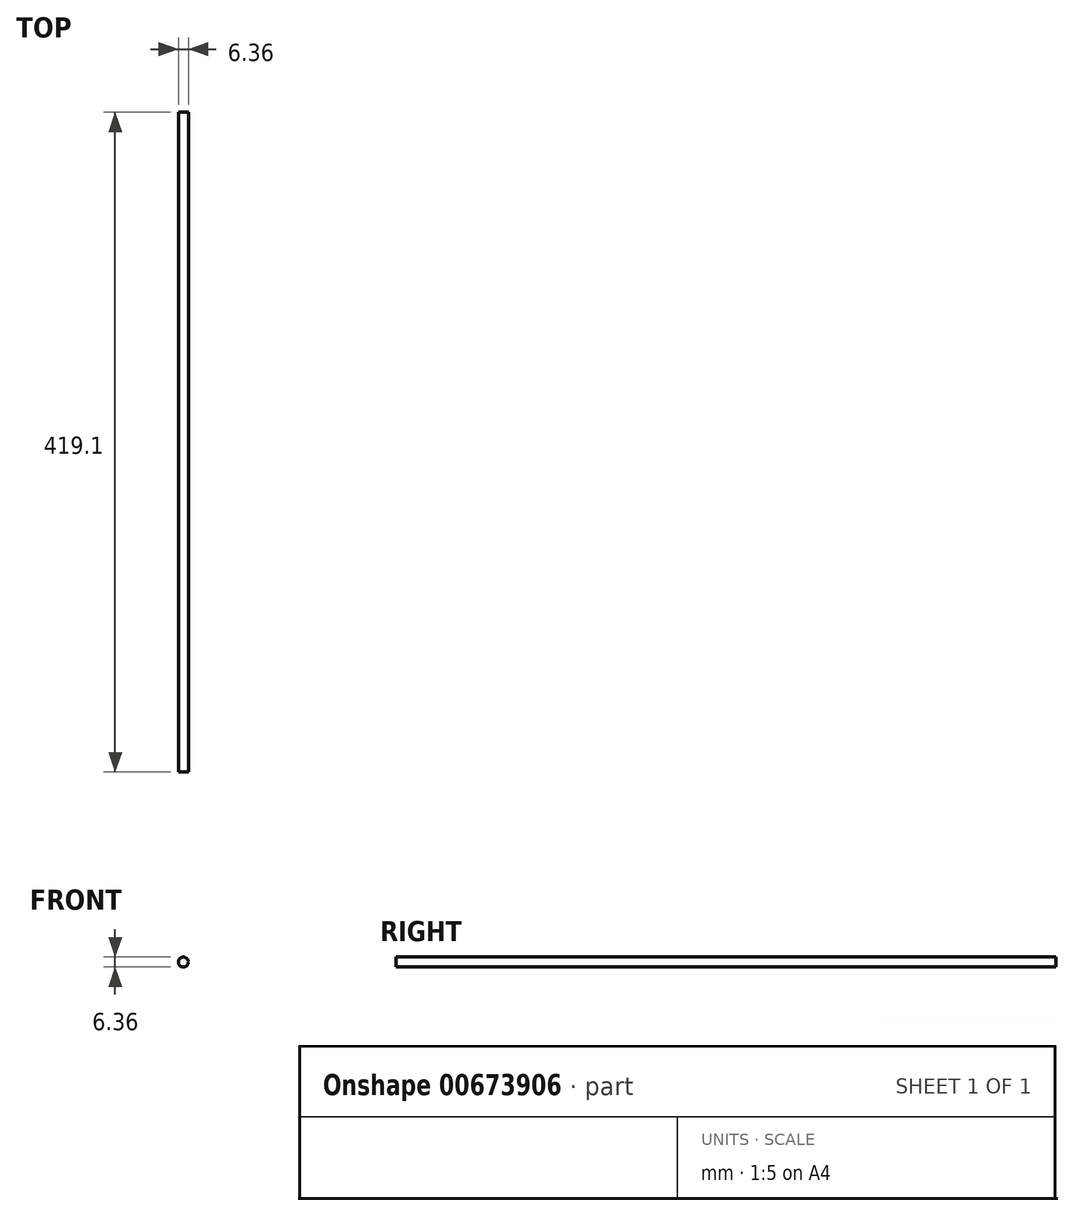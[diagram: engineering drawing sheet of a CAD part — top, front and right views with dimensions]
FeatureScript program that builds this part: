
annotation { "Feature Type Name" : "Feature", "Feature Type Description" : "" }
export const myFeature = defineFeature(function(context is Context, id is Id, definition is map)
    precondition{}
    {
        {
            var Q0;
            Q0=qCreatedBy(makeId("Front.planeOp"),FACE);
            var sketch = newSketch(context, id + "F0", { "sketchPlane" : qUnion([Q0])});
            skCircle(sketch, "E0", {"center": v(0, 0) * mm, "radius": 3.18 * mm});
            skSolve(sketch);
        }
        {
            var Q0;
            Q0 = qSketchRegion(id + "F0", true);
            extrude(context, id + "F1", {"entities" : qUnion([Q0]), "endBound" : BoundingType.SYMMETRIC, "depth" : 419.1 * mm, "offsetDistance" : 25.4 * mm});
        }
    });
